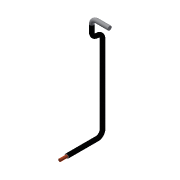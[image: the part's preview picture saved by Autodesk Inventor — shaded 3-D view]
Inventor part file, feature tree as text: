
AUTODESK INVENTOR PART (.ipt)
format: ipt  version: 2016 SP2 (Build 200236200, 236)  size: 132,608 bytes
history: native  units: mm
features: sketch x4, extrude x2, sweep x1
ambient origin geometry x8: Origin, YZ Plane, XZ Plane, XY Plane, X Axis, Y Axis, Z Axis, Center Point
bodies: Body1 (feature_tree)
feature tree (7):
  extrude  "Extrusion3"  Depth=30.0mm
  sweep  "Sweep1"
  extrude  "Extrusion4"  Depth=40.0mm TaperAngle=0.0deg
  sketch  "3D Sketch1"
  sketch  "Sketch2"  dims[d4=30.0mm d5=30.0mm]
  sketch  "Sketch3"  dims[d6=30.0mm d7=30.0mm]
  sketch  "Sketch4"  dims[d8=15.0mm d9=40.0mm d10=0.0mm d11=22.5mm d12=200.0mm d13=600.0mm d14=60.0mm d15=130.0mm d17=0.0mm d18=0.0mm d19=60.0mm d20=30.0mm d21=15.0mm d22=30.0mm d23=0.0mm]
